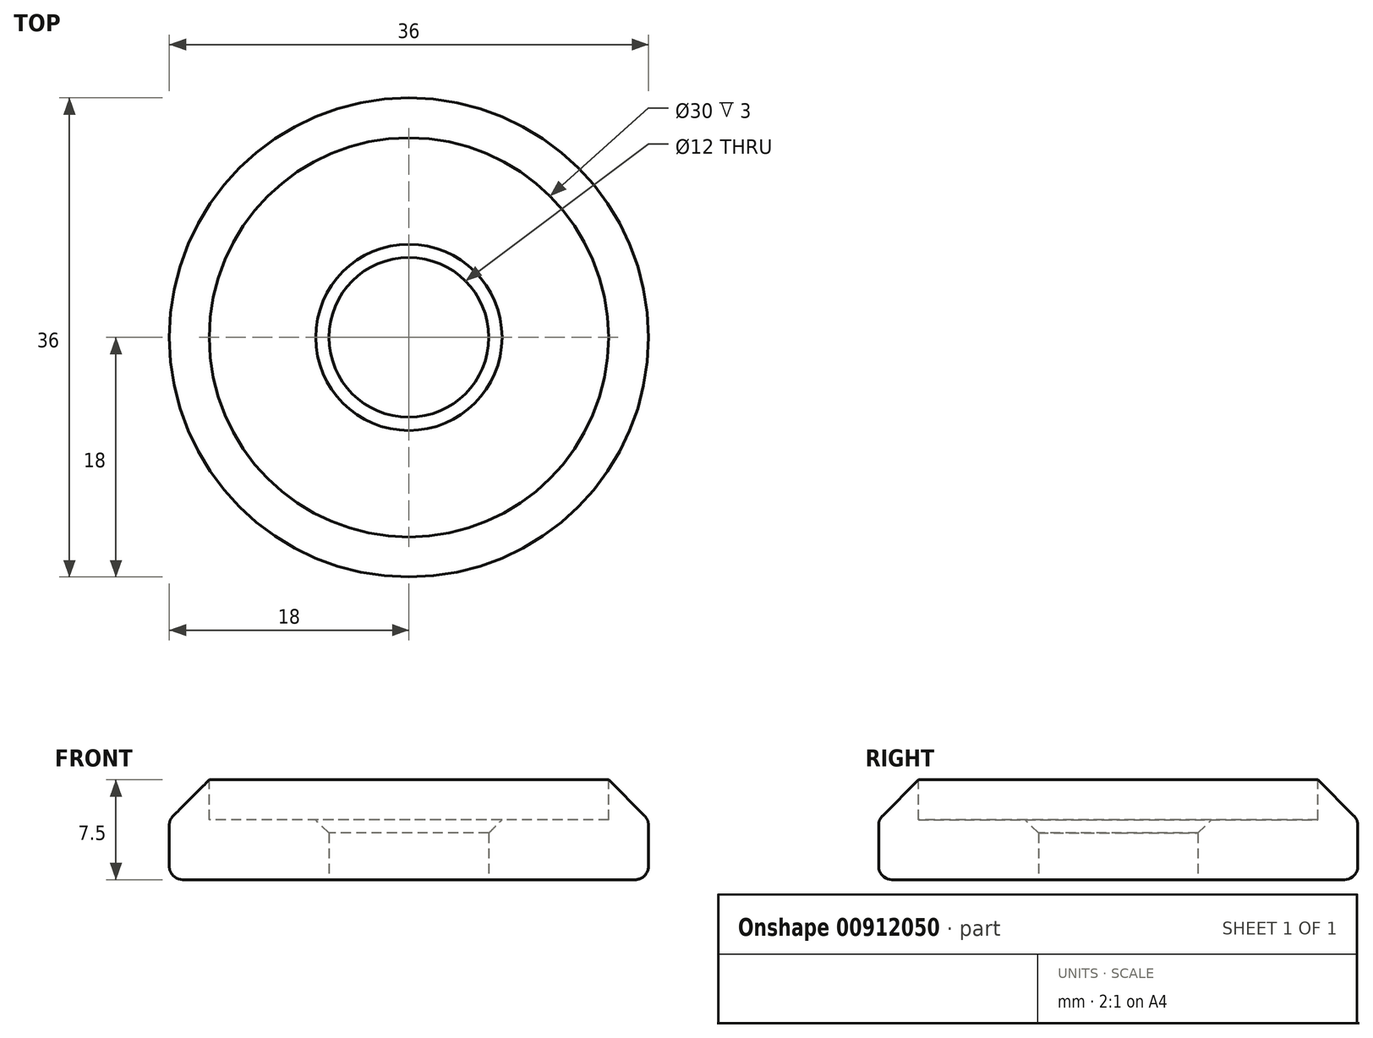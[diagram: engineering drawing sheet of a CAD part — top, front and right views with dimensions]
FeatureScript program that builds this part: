
annotation { "Feature Type Name" : "Feature", "Feature Type Description" : "" }
export const myFeature = defineFeature(function(context is Context, id is Id, definition is map)
    precondition{}
    {
        {
            var Q0;
            Q0=qCreatedBy(makeId("Top.planeOp"),FACE);
            var sketch = newSketch(context, id + "F0", { "sketchPlane" : qUnion([Q0])});
            skCircle(sketch, "E0", {"center": v(0, 0) * mm, "radius": 18 * mm});
            skSolve(sketch);
        }
        {
            var Q0;
            Q0=makeQuery(id+"F0.imprint","IMPRINT",FACE,{"disambiguationData":[TD([[makeQuery(id+"F0.imprint","IMPRINT",EDGE,{"derivedFrom":sQuery(id+"F0.wireOp",EDGE,"E0")}),1.0]])]});
            extrude(context, id + "F1", {"entities" : qUnion([Q0]), "depth" : 9.5 * mm, "offsetDistance" : 25 * mm});
        }
        {
            var Q0;
            Q0=makeQuery(id+"F1.opExtrude","CAP_FACE",FACE,{"disambiguationData":[OSD([sQuery(id+"F0.wireOp",EDGE,"E0")])],"isStart":false});
            var sketch = newSketch(context, id + "F2", { "sketchPlane" : qUnion([Q0])});
            skCircle(sketch, "E1", {"center": v(0, 0) * mm, "radius": 15 * mm});
            skSolve(sketch);
        }
        {
            var Q0;
            Q0 = qSketchRegion(id + "F2", true);
            extrude(context, id + "F3", {"entities" : qUnion([Q0]), "operationType" : NewBodyOperationType.REMOVE, "oppositeDirection" : true, "depth" : 5 * mm, "offsetDistance" : 25 * mm});
        }
        {
            var Q0;
            Q0=qCreatedBy(makeId("Top.planeOp"),FACE);
            var sketch = newSketch(context, id + "F4", { "sketchPlane" : qUnion([Q0])});
            skCircle(sketch, "E2", {"center": v(0, 0) * mm, "radius": 6 * mm});
            skSolve(sketch);
        }
        {
            var Q0;
            Q0 = qSketchRegion(id + "F4", true);
            extrude(context, id + "F5", {"entities" : qUnion([Q0]), "operationType" : NewBodyOperationType.REMOVE, "depth" : 5 * mm, "offsetDistance" : 25 * mm});
        }
        {
            var Q0;
            Q0=makeQuery(id+"F5.boolean.opBoolean","INTERSECT",EDGE,{"derivedFrom":[makeQuery(id+"F3.boolean.opBoolean","COPY",FACE,{"derivedFrom":makeQuery(id+"F3.opExtrude","CAP_FACE",FACE,{"disambiguationData":[OSD([sQuery(id+"F2.wireOp",EDGE,"E1")])],"isStart":false})}),makeQuery(id+"F5.opExtrude","SWEPT_FACE",FACE,{"disambiguationData":[OSD([sQuery(id+"F4.wireOp",EDGE,"E2")])]})]});
            chamfer(context, id + "F6", {"entities" : qUnion([Q0]), "width" : 1 * mm, "tangentPropagation" : true});
        }
        {
            var Q0;
            Q0=makeQuery(id+"F1.opExtrude","CAP_EDGE",EDGE,{"disambiguationData":[OSD([sQuery(id+"F0.wireOp",EDGE,"E0")])],"isStart":false});
            chamfer(context, id + "F7", {"entities" : qUnion([Q0]), "width" : 5 * mm, "tangentPropagation" : true});
        }
        {
            var Q0;
            {var subQ0=sQuery(id+"F0.wireOp",EDGE,"E0");Q0=makeQuery(id+"F7.opChamfer","BLEND_EDGE",EDGE,{"blendedFrom":[makeQuery(id+"F1.opExtrude","CAP_EDGE",EDGE,{"disambiguationData":[OSD([subQ0])],"isStart":false}),makeQuery(id+"F1.opExtrude","SWEPT_FACE",FACE,{"disambiguationData":[OSD([subQ0])]})],"blendedInto":[makeQuery(id+"F1.opExtrude","SWEPT_FACE",FACE,{"disambiguationData":[OSD([subQ0])]})]});}
            fillet(context, id + "F8", {"entities" : qUnion([Q0]), "radius" : 1 * mm, "tangentPropagation" : true, "allowEdgeOverflow" : false});
        }
        {
            var Q0;
            Q0=makeQuery(id+"F1.opExtrude","CAP_EDGE",EDGE,{"disambiguationData":[OSD([sQuery(id+"F0.wireOp",EDGE,"E0")])],"isStart":true});
            fillet(context, id + "F9", {"entities" : qUnion([Q0]), "radius" : 1 * mm, "tangentPropagation" : true, "allowEdgeOverflow" : false});
        }
    });
